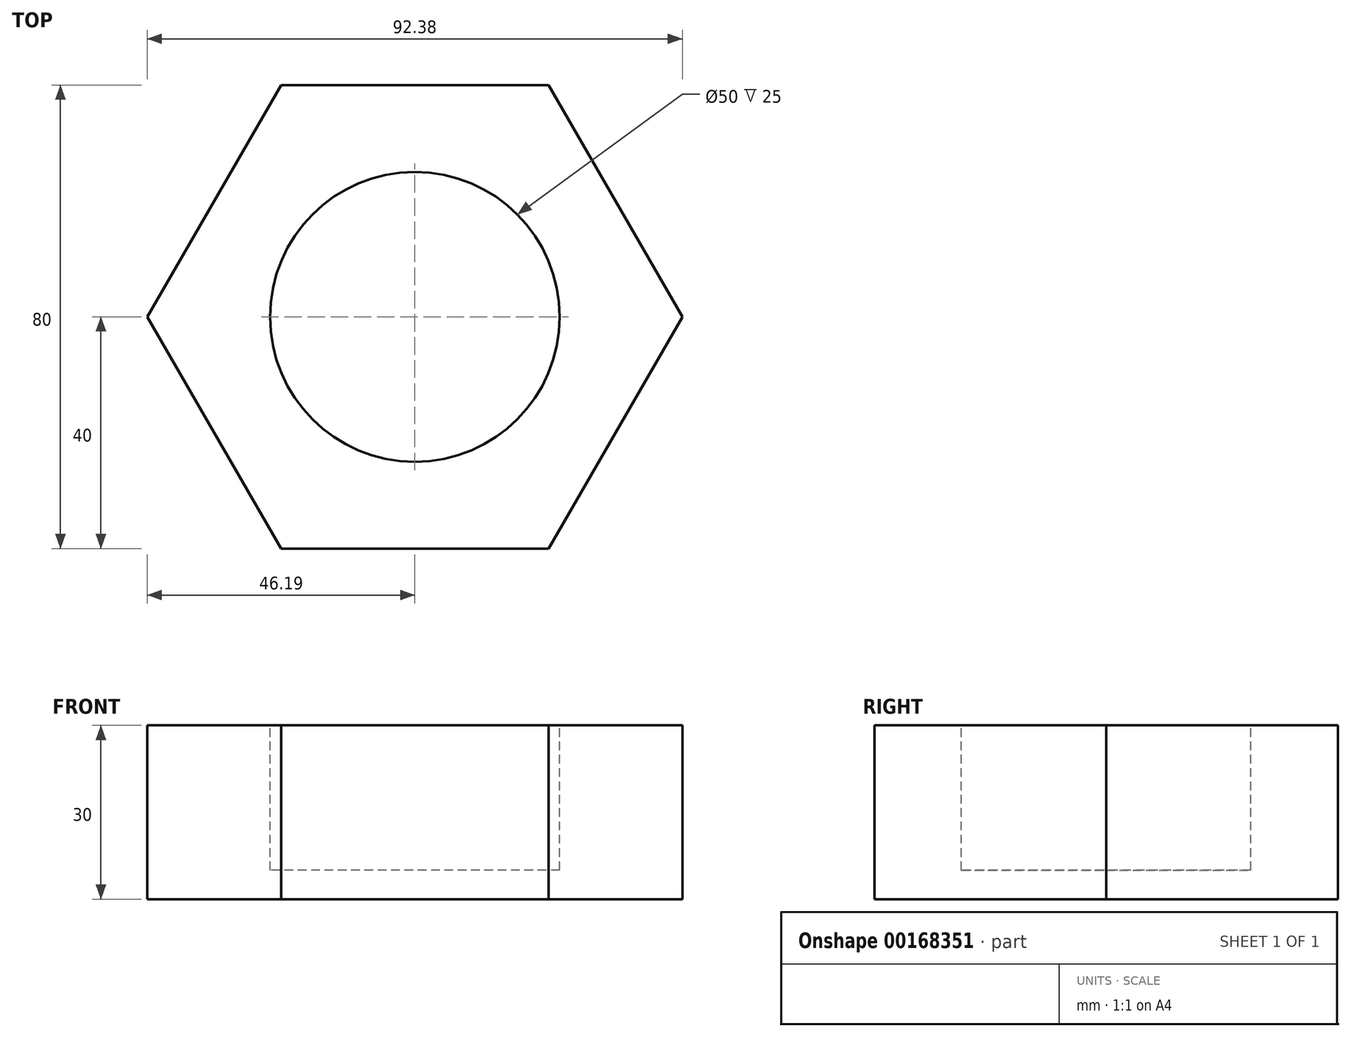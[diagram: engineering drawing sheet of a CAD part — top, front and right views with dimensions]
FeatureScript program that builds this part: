
annotation { "Feature Type Name" : "Feature", "Feature Type Description" : "" }
export const myFeature = defineFeature(function(context is Context, id is Id, definition is map)
    precondition{}
    {
        {
            var Q0;
            Q0=qCreatedBy(makeId("Top.planeOp"),FACE);
            var sketch = newSketch(context, id + "F0", { "sketchPlane" : qUnion([Q0])});
            skCircle(sketch, "E0.cCircle", {"center": v(0, 0) * mm, "radius": 40 * mm, "construction": true});
            skLineSegment(sketch, "E0.0", {"start": v(-23.1, 40) * mm, "end": v(23.1, 40) * mm});
            skLineSegment(sketch, "E0.1", {"start": v(23.1, 40) * mm, "end": v(46.19, 0) * mm});
            skLineSegment(sketch, "E0.2", {"start": v(46.19, 0) * mm, "end": v(23.1, -40) * mm});
            skLineSegment(sketch, "E0.3", {"start": v(23.1, -40) * mm, "end": v(-23.1, -40) * mm});
            skLineSegment(sketch, "E0.4", {"start": v(-23.1, -40) * mm, "end": v(-46.19, 0) * mm});
            skLineSegment(sketch, "E0.5", {"start": v(-46.19, 0) * mm, "end": v(-23.1, 40) * mm});
            skPoint(sketch, "E0.0.midPoint", {"position": v(0, 40) * mm});
            skSolve(sketch);
        }
        {
            var Q0;
            Q0 = qSketchRegion(id + "F0", true);
            extrude(context, id + "F1", {"entities" : qUnion([Q0]), "depth" : 30 * mm});
        }
        {
            var Q0;
            Q0=makeQuery(id+"F1.opExtrude","CAP_FACE",FACE,{"disambiguationData":[OSD([sQuery(id+"F0.wireOp",EDGE,"E0.0"),sQuery(id+"F0.wireOp",EDGE,"E0.1"),sQuery(id+"F0.wireOp",EDGE,"E0.2"),sQuery(id+"F0.wireOp",EDGE,"E0.3"),sQuery(id+"F0.wireOp",EDGE,"E0.4"),sQuery(id+"F0.wireOp",EDGE,"E0.5")])],"isStart":false});
            var sketch = newSketch(context, id + "F2", { "sketchPlane" : qUnion([Q0])});
            skCircle(sketch, "E1", {"center": v(0, 0) * mm, "radius": 25 * mm});
            skSolve(sketch);
        }
        {
            var Q0;
            Q0=makeQuery(id+"F2.imprint","IMPRINT",FACE,{"disambiguationData":[TD([[makeQuery(id+"F2.imprint","IMPRINT",EDGE,{"derivedFrom":sQuery(id+"F2.wireOp",EDGE,"E1")}),1.0]])]});
            extrude(context, id + "F3", {"entities" : qUnion([Q0]), "operationType" : NewBodyOperationType.REMOVE, "oppositeDirection" : true, "depth" : 25 * mm});
        }
    });
